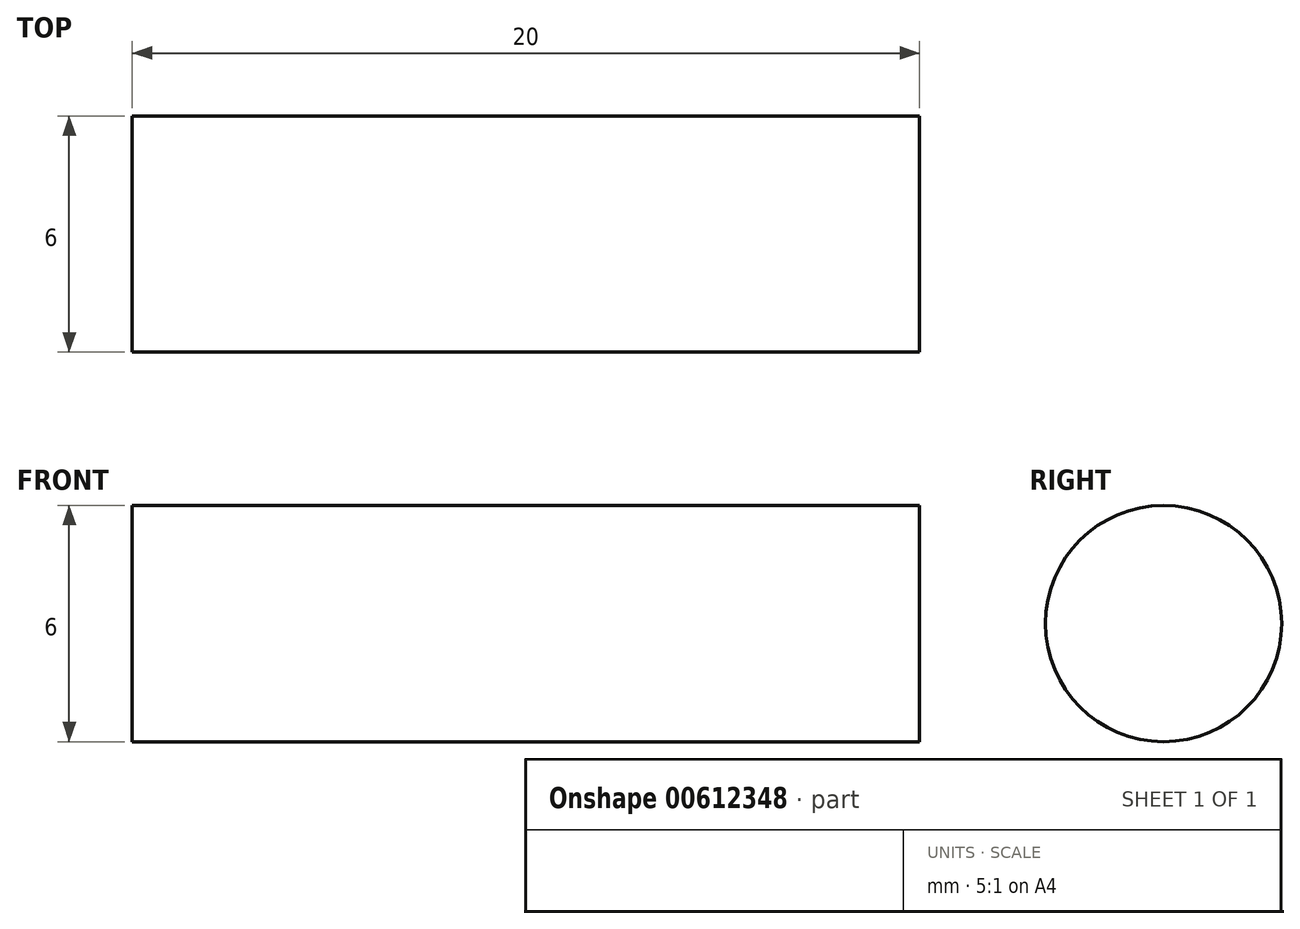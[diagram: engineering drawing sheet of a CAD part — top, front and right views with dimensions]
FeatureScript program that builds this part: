
annotation { "Feature Type Name" : "Feature", "Feature Type Description" : "" }
export const myFeature = defineFeature(function(context is Context, id is Id, definition is map)
    precondition{}
    {
        {
            var Q0;
            Q0=qCreatedBy(makeId("Right.planeOp"),FACE);
            var sketch = newSketch(context, id + "F0", { "sketchPlane" : qUnion([Q0])});
            skCircle(sketch, "E0", {"center": v(0, 0) * mm, "radius": 3 * mm});
            skSolve(sketch);
        }
        {
            var Q0;
            Q0=makeQuery(id+"F0.imprint","IMPRINT",FACE,{"disambiguationData":[TD([[makeQuery(id+"F0.imprint","IMPRINT",EDGE,{"derivedFrom":sQuery(id+"F0.wireOp",EDGE,"E0")}),1.0]])]});
            extrude(context, id + "F1", {"entities" : qUnion([Q0]), "depth" : 20 * mm, "offsetDistance" : 25 * mm});
        }
    });
